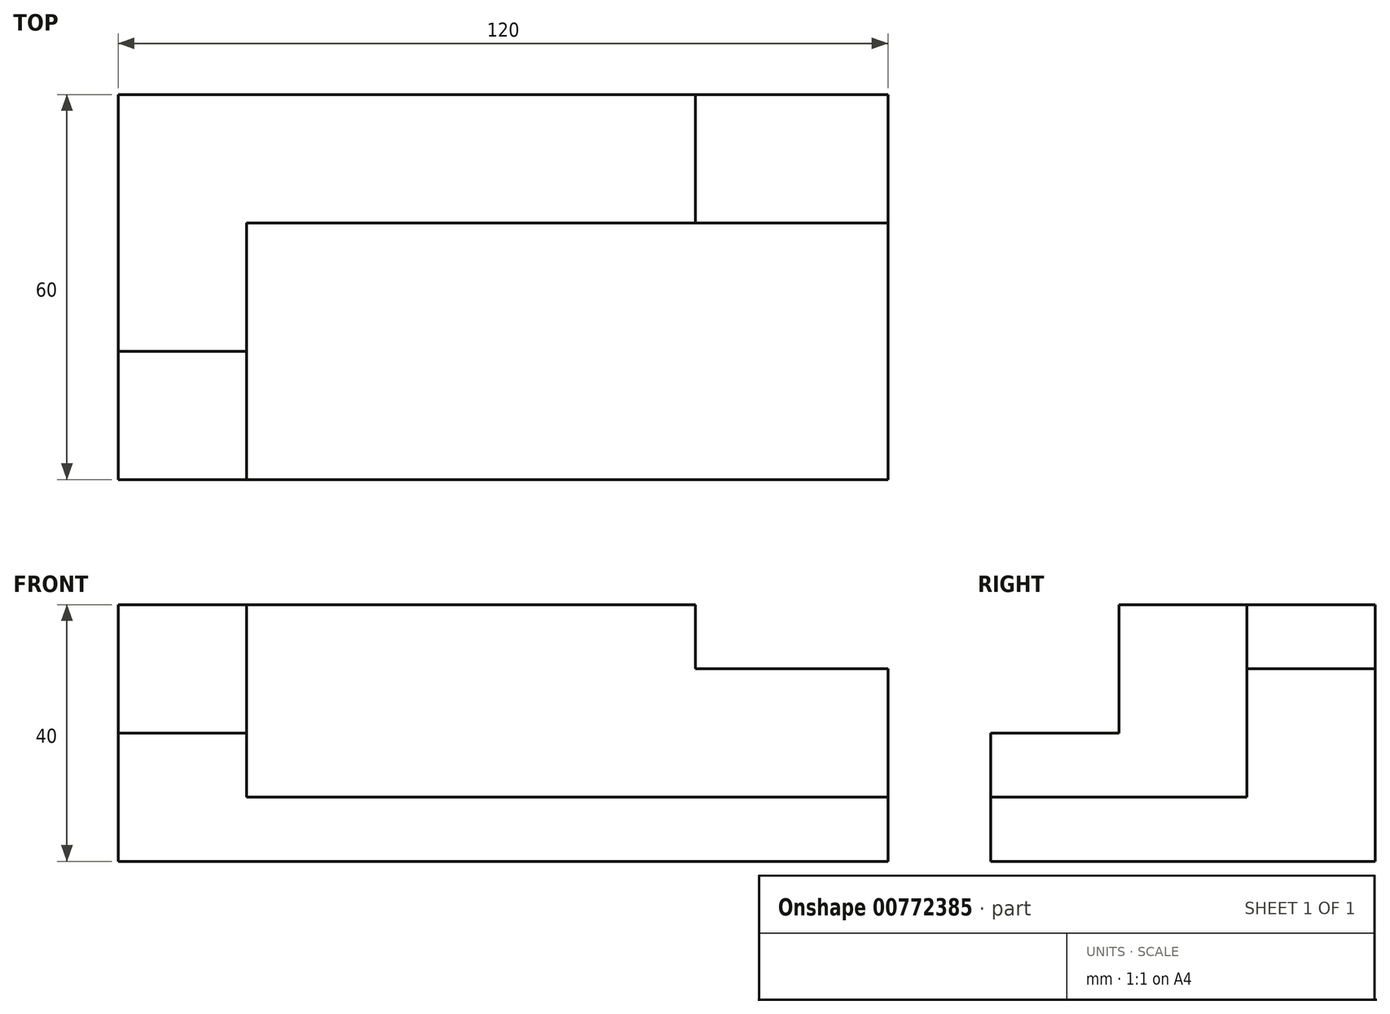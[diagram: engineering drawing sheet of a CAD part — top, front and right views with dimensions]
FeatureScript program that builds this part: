
annotation { "Feature Type Name" : "Feature", "Feature Type Description" : "" }
export const myFeature = defineFeature(function(context is Context, id is Id, definition is map)
    precondition{}
    {
        {
            var Q0;
            Q0=qCreatedBy(makeId("Top.planeOp"),FACE);
            var sketch = newSketch(context, id + "F0", { "sketchPlane" : qUnion([Q0])});
            skLineSegment(sketch, "E0", {"start": v(0, 0) * mm, "end": v(120, 0) * mm});
            skLineSegment(sketch, "E1", {"start": v(120, 0) * mm, "end": v(120, -60) * mm});
            skLineSegment(sketch, "E2", {"start": v(120, -60) * mm, "end": v(0, -60) * mm});
            skLineSegment(sketch, "E3", {"start": v(0, -60) * mm, "end": v(0, 0) * mm});
            skLineSegment(sketch, "E4", {"start": v(120, -20) * mm, "end": v(20, -20) * mm});
            skLineSegment(sketch, "E5", {"start": v(20, -20) * mm, "end": v(20, -60) * mm});
            skLineSegment(sketch, "E6", {"start": v(0, -40) * mm, "end": v(20, -40) * mm});
            skLineSegment(sketch, "E7", {"start": v(90, 0) * mm, "end": v(90, -20) * mm});
            skSolve(sketch);
        }
        {
            var Q0;
            Q0=qSketchRegion(id+"F0",true);
            extrude(context, id + "F1", {"entities" : qUnion([Q0]), "oppositeDirection" : true, "depth" : 40 * mm, "offsetDistance" : 25 * mm});
        }
        {
            var Q0;
            {var subQ5=sQuery(id+"F0.wireOp",EDGE,"E6");Q0=makeQuery(id+"F0.imprint","IMPRINT",FACE,{"disambiguationData":[TD([[makeQuery(id+"F0.imprint","IMPRINT",EDGE,{"derivedFrom":subQ5}),-1.0]])]});}
            extrude(context, id + "F2", {"entities" : qUnion([Q0]), "operationType" : NewBodyOperationType.REMOVE, "oppositeDirection" : true, "depth" : 20 * mm, "offsetDistance" : 25 * mm});
        }
        {
            var Q0;
            {var subQ3=sQuery(id+"F0.wireOp",EDGE,"E7");Q0=makeQuery(id+"F0.imprint","IMPRINT",FACE,{"disambiguationData":[TD([[makeQuery(id+"F0.imprint","IMPRINT",EDGE,{"derivedFrom":subQ3}),1.0]])]});}
            extrude(context, id + "F3", {"entities" : qUnion([Q0]), "operationType" : NewBodyOperationType.REMOVE, "oppositeDirection" : true, "depth" : 10 * mm, "offsetDistance" : 25 * mm});
        }
        {
            var Q0;
            {var subQ4=sQuery(id+"F0.wireOp",EDGE,"E2");var subQ5=sQuery(id+"F0.wireOp",EDGE,"E1");var subQ6=makeQuery(id+"F0.imprint","INTERSECT",VERTEX,{"derivedFrom":[subQ5,subQ4]});Q0=makeQuery(id+"F0.imprint","IMPRINT",FACE,{"disambiguationData":[TD([[makeQuery(id+"F0.imprint","IMPRINT",EDGE,{"disambiguationData":[TD([[subQ6,1.0]])],"derivedFrom":subQ5}),-1.0]])]});}
            extrude(context, id + "F4", {"entities" : qUnion([Q0]), "operationType" : NewBodyOperationType.REMOVE, "oppositeDirection" : true, "depth" : 30 * mm, "offsetDistance" : 25 * mm});
        }
    });
